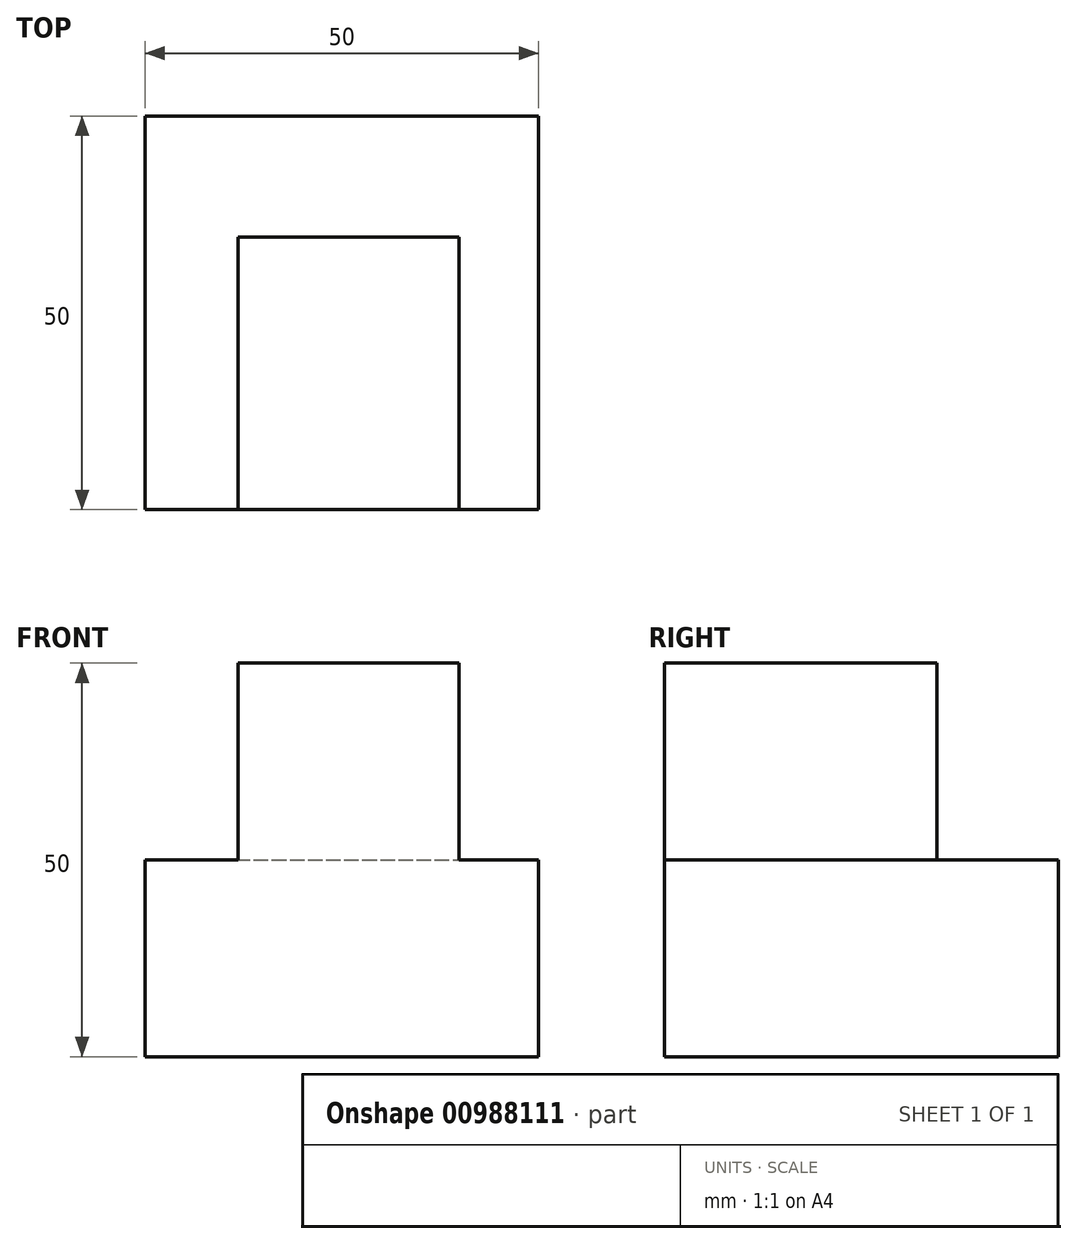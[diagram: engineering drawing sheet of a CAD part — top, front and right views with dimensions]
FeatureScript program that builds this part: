
annotation { "Feature Type Name" : "Feature", "Feature Type Description" : "" }
export const myFeature = defineFeature(function(context is Context, id is Id, definition is map)
    precondition{}
    {
        {
            var Q0;
            Q0=qCreatedBy(makeId("Top.planeOp"),FACE);
            var sketch = newSketch(context, id + "F0", { "sketchPlane" : qUnion([Q0])});
            skLineSegment(sketch, "E0.bottom", {"start": v(0, 0) * mm, "end": v(50, 0) * mm});
            skLineSegment(sketch, "E0.top", {"start": v(0, 50) * mm, "end": v(50, 50) * mm});
            skLineSegment(sketch, "E0.left", {"start": v(0, 0) * mm, "end": v(0, 50) * mm});
            skLineSegment(sketch, "E0.right", {"start": v(50, 0) * mm, "end": v(50, 50) * mm});
            skSolve(sketch);
        }
        {
            var Q0;
            Q0=makeQuery(id+"F0.imprint","IMPRINT",FACE,{"disambiguationData":[TD([[makeQuery(id+"F0.imprint","IMPRINT",EDGE,{"derivedFrom":sQuery(id+"F0.wireOp",EDGE,"E0.bottom")}),1.0]])]});
            extrude(context, id + "F1", {"entities" : qUnion([Q0]), "depth" : 25 * mm, "offsetDistance" : 25 * mm});
        }
        {
            var Q0;
            Q0=makeQuery(id+"F1.opExtrude","CAP_FACE",FACE,{"disambiguationData":[OSD([sQuery(id+"F0.wireOp",EDGE,"E0.bottom"),sQuery(id+"F0.wireOp",EDGE,"E0.top"),sQuery(id+"F0.wireOp",EDGE,"E0.left"),sQuery(id+"F0.wireOp",EDGE,"E0.right")])],"isStart":false});
            var sketch = newSketch(context, id + "F2", { "sketchPlane" : qUnion([Q0])});
            skLineSegment(sketch, "E1.bottom", {"start": v(11.85, 34.6) * mm, "end": v(39.91, 34.6) * mm});
            skLineSegment(sketch, "E1.top", {"start": v(11.85, 13.97) * mm, "end": v(39.91, 13.97) * mm});
            skLineSegment(sketch, "E1.left", {"start": v(11.85, 34.6) * mm, "end": v(11.85, 13.97) * mm});
            skLineSegment(sketch, "E1.right", {"start": v(39.91, 34.6) * mm, "end": v(39.91, 13.97) * mm});
            skSolve(sketch);
        }
        {
            var Q0;
            Q0=makeQuery(id+"F2.imprint","IMPRINT",FACE,{"disambiguationData":[TD([[makeQuery(id+"F2.imprint","IMPRINT",EDGE,{"derivedFrom":sQuery(id+"F2.wireOp",EDGE,"E1.bottom")}),-1.0]])]});
            extrude(context, id + "F3", {"entities" : qUnion([Q0]), "operationType" : NewBodyOperationType.ADD, "depth" : 25 * mm, "offsetDistance" : 25 * mm});
        }
        {
            var Q0;
            Q0=makeQuery(id+"F3.opExtrude","SWEPT_FACE",FACE,{"disambiguationData":[OSD([sQuery(id+"F2.wireOp",EDGE,"E1.top")])]});
            var Q1;
            Q1=makeQuery(id+"F1.opExtrude","SWEPT_FACE",FACE,{"disambiguationData":[OSD([sQuery(id+"F0.wireOp",EDGE,"E0.bottom")])]});
            extrude(context, id + "F4", {"entities" : qUnion([Q0]), "operationType" : NewBodyOperationType.ADD, "endBound" : BoundingType.UP_TO_SURFACE, "depth" : 25 * mm, "endBoundEntityFace" : qUnion([Q1]), "offsetDistance" : 25 * mm});
        }
    });
